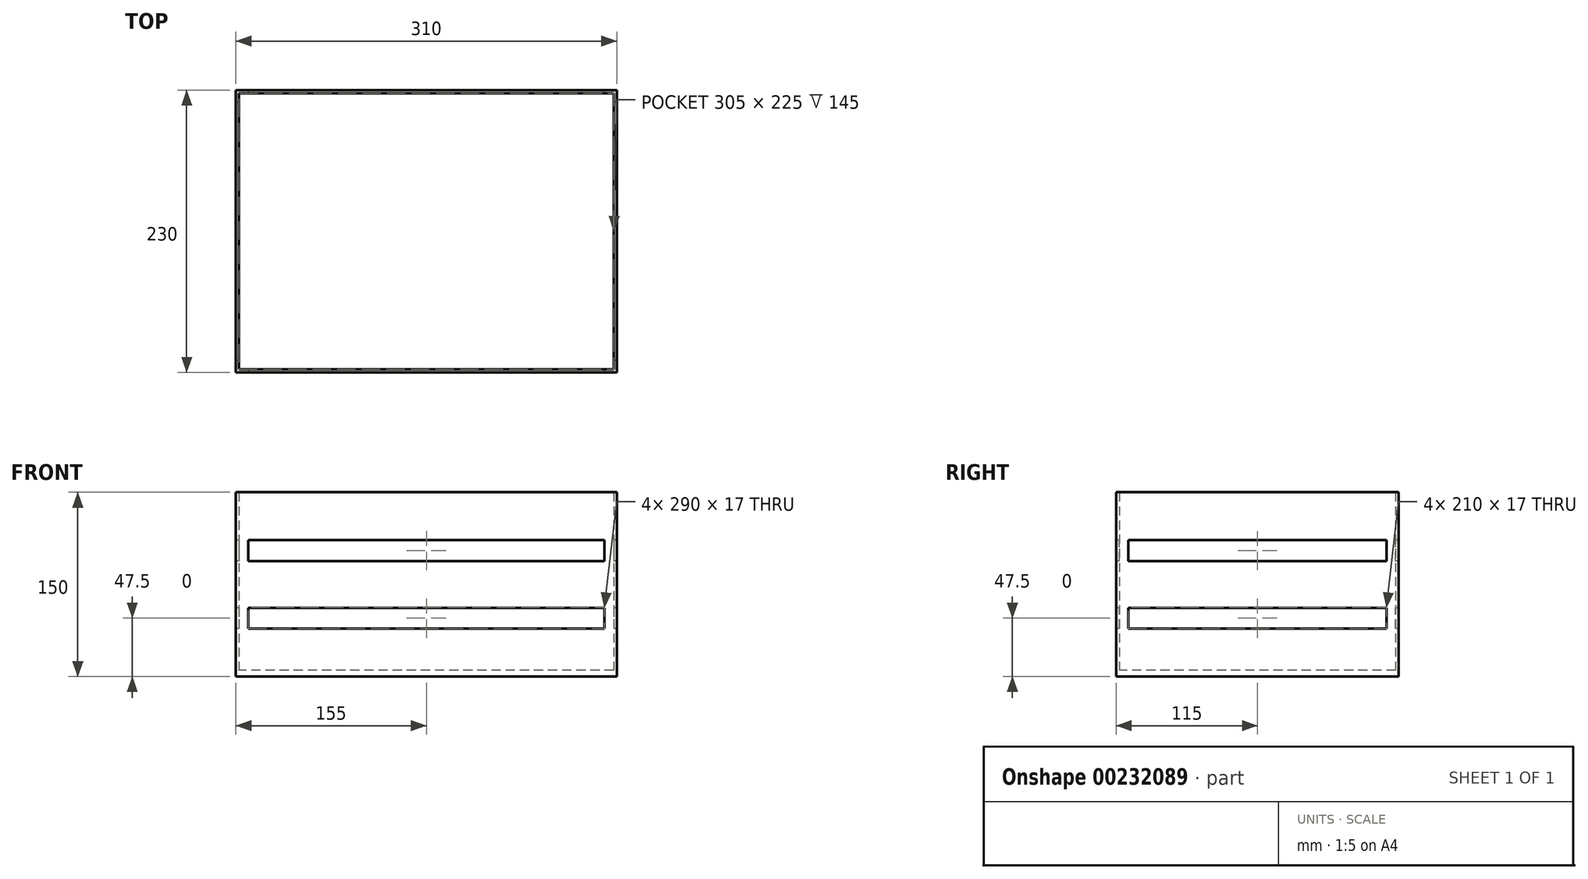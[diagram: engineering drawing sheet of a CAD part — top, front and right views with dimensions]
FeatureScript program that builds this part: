
annotation { "Feature Type Name" : "Feature", "Feature Type Description" : "" }
export const myFeature = defineFeature(function(context is Context, id is Id, definition is map)
    precondition{}
    {
        {
            var Q0;
            Q0=qCreatedBy(makeId("Top.planeOp"),FACE);
            var sketch = newSketch(context, id + "F0", { "sketchPlane" : qUnion([Q0])});
            skLineSegment(sketch, "E0.bottom", {"start": v(-155, 115) * mm, "end": v(155, 115) * mm});
            skLineSegment(sketch, "E0.top", {"start": v(-155, -115) * mm, "end": v(155, -115) * mm});
            skLineSegment(sketch, "E0.left", {"start": v(-155, 115) * mm, "end": v(-155, -115) * mm});
            skLineSegment(sketch, "E0.right", {"start": v(155, 115) * mm, "end": v(155, -115) * mm});
            skSolve(sketch);
        }
        {
            var Q0;
            Q0=makeQuery(id+"F0.imprint","IMPRINT",FACE,{"disambiguationData":[TD([[makeQuery(id+"F0.imprint","IMPRINT",EDGE,{"derivedFrom":sQuery(id+"F0.wireOp",EDGE,"E0.bottom")}),-1.0]])]});
            extrude(context, id + "F1", {"entities" : qUnion([Q0]), "depth" : 5 * mm});
        }
        {
            var Q0;
            Q0=makeQuery(id+"F1.opExtrude","CAP_FACE",FACE,{"disambiguationData":[OSD([sQuery(id+"F0.wireOp",EDGE,"E0.bottom"),sQuery(id+"F0.wireOp",EDGE,"E0.top"),sQuery(id+"F0.wireOp",EDGE,"E0.left"),sQuery(id+"F0.wireOp",EDGE,"E0.right")])],"isStart":true});
            var sketch = newSketch(context, id + "F2", { "sketchPlane" : qUnion([Q0])});
            skLineSegment(sketch, "E1.0.0", {"start": v(-155, 115) * mm, "end": v(-155, -115) * mm});
            skLineSegment(sketch, "E1.0.1", {"start": v(-155, -115) * mm, "end": v(155, -115) * mm});
            skLineSegment(sketch, "E1.0.2", {"start": v(155, -115) * mm, "end": v(155, 115) * mm});
            skLineSegment(sketch, "E1.0.3", {"start": v(155, 115) * mm, "end": v(-155, 115) * mm});
            skLineSegment(sketch, "E2.bottom", {"start": v(-152.5, 112.5) * mm, "end": v(152.5, 112.5) * mm});
            skLineSegment(sketch, "E2.top", {"start": v(-152.5, -112.5) * mm, "end": v(152.5, -112.5) * mm});
            skLineSegment(sketch, "E2.left", {"start": v(-152.5, 112.5) * mm, "end": v(-152.5, -112.5) * mm});
            skLineSegment(sketch, "E2.right", {"start": v(152.5, 112.5) * mm, "end": v(152.5, -112.5) * mm});
            skSolve(sketch);
        }
        {
            var Q0;
            Q0=makeQuery(id+"F2.imprint","IMPRINT",FACE,{"disambiguationData":[TD([[makeQuery(id+"F2.imprint","IMPRINT",EDGE,{"derivedFrom":sQuery(id+"F2.wireOp",EDGE,"E1.0.0")}),-1.0]])]});
            extrude(context, id + "F3", {"entities" : qUnion([Q0]), "operationType" : NewBodyOperationType.ADD, "oppositeDirection" : true, "depth" : 150 * mm});
        }
        {
            var Q0;
            Q0=makeQuery(id+"F3.boolean.opBoolean","MERGE",FACE,{"derivedFrom":[makeQuery(id+"F1.opExtrude","SWEPT_FACE",FACE,{"disambiguationData":[OSD([sQuery(id+"F0.wireOp",EDGE,"E0.left")])]}),makeQuery(id+"F3.opExtrude","SWEPT_FACE",FACE,{"disambiguationData":[OSD([sQuery(id+"F2.wireOp",EDGE,"E1.0.0")])]})]});
            var sketch = newSketch(context, id + "F4", { "sketchPlane" : qUnion([Q0])});
            skLineSegment(sketch, "E3.0.0", {"start": v(-115, 0) * mm, "end": v(115, 0) * mm, "construction": true});
            skLineSegment(sketch, "E3.0.1", {"start": v(115, 0) * mm, "end": v(115, 150) * mm, "construction": true});
            skLineSegment(sketch, "E3.0.2", {"start": v(115, 150) * mm, "end": v(-115, 150) * mm, "construction": true});
            skLineSegment(sketch, "E3.0.3", {"start": v(-115, 150) * mm, "end": v(-115, 0) * mm, "construction": true});
            skLineSegment(sketch, "E4.bottom", {"start": v(-105, 111) * mm, "end": v(105, 111) * mm});
            skLineSegment(sketch, "E4.top", {"start": v(-105, 94) * mm, "end": v(105, 94) * mm});
            skLineSegment(sketch, "E4.left", {"start": v(-105, 111) * mm, "end": v(-105, 94) * mm});
            skLineSegment(sketch, "E4.right", {"start": v(105, 111) * mm, "end": v(105, 94) * mm});
            skLineSegment(sketch, "E5.bottom", {"start": v(-105, 56) * mm, "end": v(105, 56) * mm});
            skLineSegment(sketch, "E5.top", {"start": v(-105, 39) * mm, "end": v(105, 39) * mm});
            skLineSegment(sketch, "E5.left", {"start": v(-105, 56) * mm, "end": v(-105, 39) * mm});
            skLineSegment(sketch, "E5.right", {"start": v(105, 56) * mm, "end": v(105, 39) * mm});
            skSolve(sketch);
        }
        {
            var Q0;
            Q0=makeQuery(id+"F4.imprint","IMPRINT",FACE,{"disambiguationData":[TD([[makeQuery(id+"F4.imprint","IMPRINT",EDGE,{"derivedFrom":sQuery(id+"F4.wireOp",EDGE,"E4.bottom")}),-1.0]])]});
            var Q1;
            Q1=makeQuery(id+"F4.imprint","IMPRINT",FACE,{"disambiguationData":[TD([[makeQuery(id+"F4.imprint","IMPRINT",EDGE,{"derivedFrom":sQuery(id+"F4.wireOp",EDGE,"E5.bottom")}),-1.0]])]});
            extrude(context, id + "F5", {"entities" : qUnion([Q0, Q1]), "operationType" : NewBodyOperationType.REMOVE, "endBound" : BoundingType.THROUGH_ALL, "oppositeDirection" : true, "depth" : 25 * mm});
        }
        {
            var Q0;
            Q0=makeQuery(id+"F3.boolean.opBoolean","MERGE",FACE,{"derivedFrom":[makeQuery(id+"F1.opExtrude","SWEPT_FACE",FACE,{"disambiguationData":[OSD([sQuery(id+"F0.wireOp",EDGE,"E0.top")])]}),makeQuery(id+"F3.opExtrude","SWEPT_FACE",FACE,{"disambiguationData":[OSD([sQuery(id+"F2.wireOp",EDGE,"E1.0.3")])]})]});
            var sketch = newSketch(context, id + "F6", { "sketchPlane" : qUnion([Q0])});
            skLineSegment(sketch, "E6.bottom", {"start": v(-145, 111) * mm, "end": v(145, 111) * mm});
            skLineSegment(sketch, "E6.top", {"start": v(-145, 94) * mm, "end": v(145, 94) * mm});
            skLineSegment(sketch, "E6.left", {"start": v(-145, 111) * mm, "end": v(-145, 94) * mm});
            skLineSegment(sketch, "E6.right", {"start": v(145, 111) * mm, "end": v(145, 94) * mm});
            skLineSegment(sketch, "E7.bottom", {"start": v(-145, 56) * mm, "end": v(145, 56) * mm});
            skLineSegment(sketch, "E7.top", {"start": v(-145, 39) * mm, "end": v(145, 39) * mm});
            skLineSegment(sketch, "E7.left", {"start": v(-145, 56) * mm, "end": v(-145, 39) * mm});
            skLineSegment(sketch, "E7.right", {"start": v(145, 56) * mm, "end": v(145, 39) * mm});
            skSolve(sketch);
        }
        {
            var Q0;
            Q0=makeQuery(id+"F6.imprint","IMPRINT",FACE,{"disambiguationData":[TD([[makeQuery(id+"F6.imprint","IMPRINT",EDGE,{"derivedFrom":sQuery(id+"F6.wireOp",EDGE,"E6.bottom")}),-1.0]])]});
            var Q1;
            Q1=makeQuery(id+"F6.imprint","IMPRINT",FACE,{"disambiguationData":[TD([[makeQuery(id+"F6.imprint","IMPRINT",EDGE,{"derivedFrom":sQuery(id+"F6.wireOp",EDGE,"E7.bottom")}),-1.0]])]});
            extrude(context, id + "F7", {"entities" : qUnion([Q0, Q1]), "operationType" : NewBodyOperationType.REMOVE, "endBound" : BoundingType.THROUGH_ALL, "oppositeDirection" : true, "depth" : 25 * mm});
        }
    });
